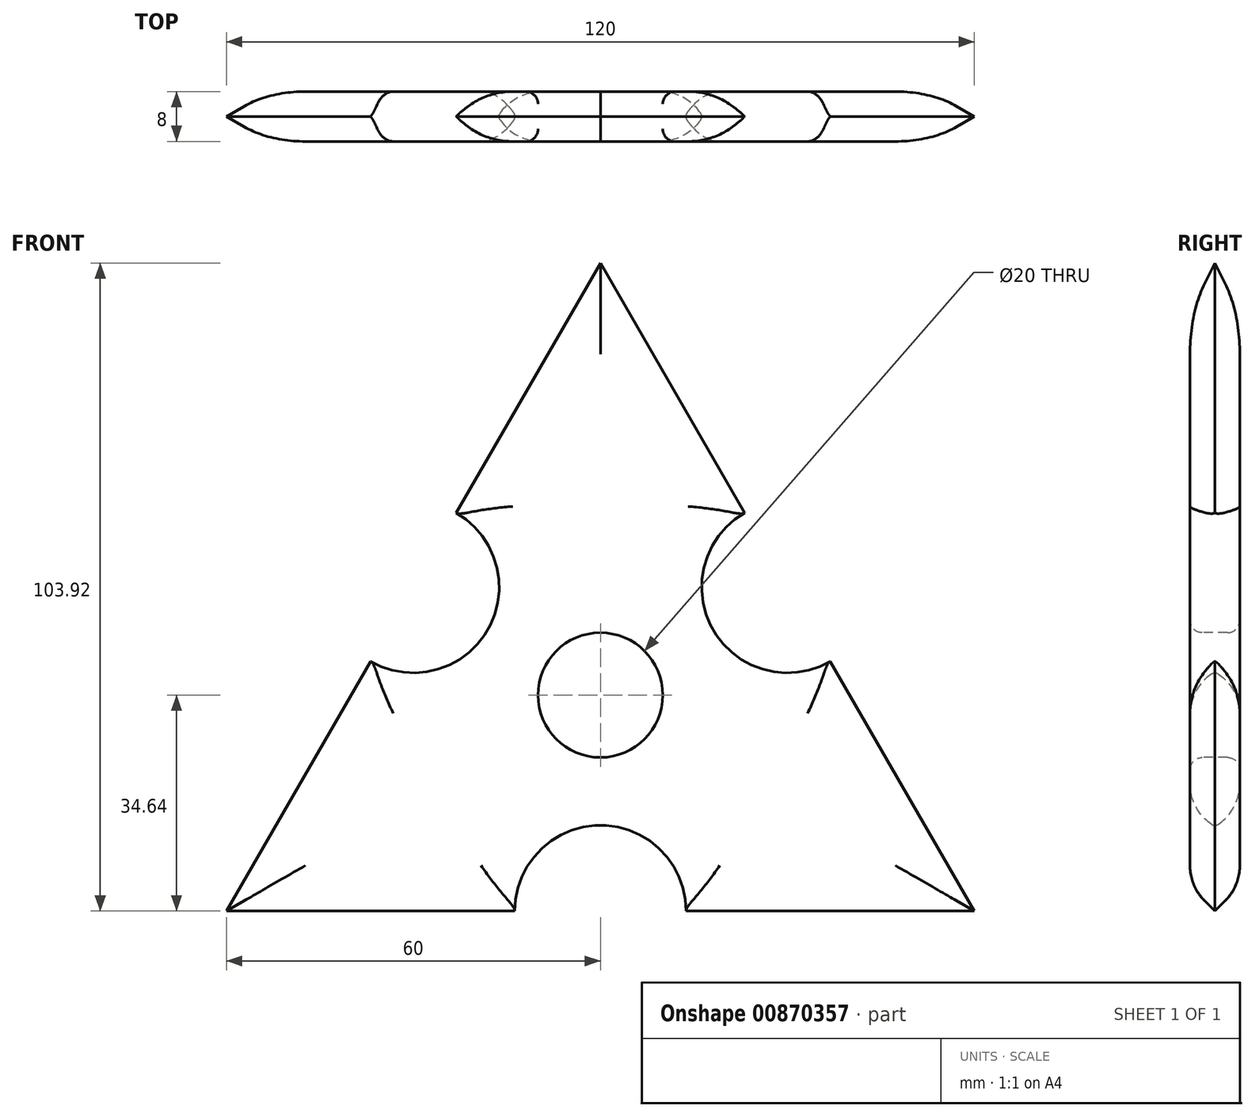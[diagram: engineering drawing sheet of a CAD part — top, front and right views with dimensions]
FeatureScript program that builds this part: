
annotation { "Feature Type Name" : "Feature", "Feature Type Description" : "" }
export const myFeature = defineFeature(function(context is Context, id is Id, definition is map)
    precondition{}
    {
        {
            var Q0;
            Q0=qCreatedBy(makeId("Front.planeOp"),FACE);
            var sketch = newSketch(context, id + "F0", { "sketchPlane" : qUnion([Q0])});
            skCircle(sketch, "E0.cCircle", {"center": v(0, 0) * mm, "radius": 69.28 * mm, "construction": true});
            skLineSegment(sketch, "E0.0", {"start": v(-60, -34.64) * mm, "end": v(0, 69.28) * mm});
            skLineSegment(sketch, "E0.1", {"start": v(0, 69.28) * mm, "end": v(60, -34.64) * mm});
            skLineSegment(sketch, "E0.2", {"start": v(60, -34.64) * mm, "end": v(-60, -34.64) * mm});
            skCircle(sketch, "E1", {"center": v(30, 17.32) * mm, "radius": 12.5 * mm});
            skCircle(sketch, "E2", {"center": v(-30, 17.32) * mm, "radius": 12.5 * mm});
            skCircle(sketch, "E3", {"center": v(0, -34.64) * mm, "radius": 12.5 * mm});
            skSolve(sketch);
        }
        {
            var Q0;
            {var subQ1=sQuery(id+"F0.wireOp",EDGE,"E0.0");var subQ8=sQuery(id+"F0.wireOp",EDGE,"E0.2");var subQ13=makeQuery(id+"F0.imprint","INTERSECT",VERTEX,{"derivedFrom":[subQ1,subQ8]});Q0=makeQuery(id+"F0.imprint","IMPRINT",FACE,{"disambiguationData":[TD([[makeQuery(id+"F0.imprint","IMPRINT",EDGE,{"disambiguationData":[TD([[subQ13,-1.0]])],"derivedFrom":subQ1}),-1.0]])]});}
            extrude(context, id + "F1", {"entities" : qUnion([Q0]), "depth" : 8 * mm, "offsetDistance" : 25 * mm, "symmetric" : true});
        }
        {
            var Q0;
            {var subQ0=sQuery(id+"F0.wireOp",EDGE,"E0.1");Q0=makeQuery(id+"F1.opExtrude","CAP_EDGE",EDGE,{"disambiguationData":[OSD([subQ0]),TDD([makeQuery(id+"F0.imprint","IMPRINT",EDGE,{"disambiguationData":[TD([[makeQuery(id+"F0.imprint","INTERSECT",VERTEX,{"derivedFrom":[sQuery(id+"F0.wireOp",EDGE,"E0.0"),subQ0]}),-1.0]])],"derivedFrom":subQ0})])],"isStart":true});}
            var Q1;
            {var subQ0=sQuery(id+"F0.wireOp",EDGE,"E0.0");Q1=makeQuery(id+"F1.opExtrude","CAP_EDGE",EDGE,{"disambiguationData":[OSD([subQ0]),TDD([makeQuery(id+"F0.imprint","IMPRINT",EDGE,{"disambiguationData":[TD([[makeQuery(id+"F0.imprint","INTERSECT",VERTEX,{"derivedFrom":[subQ0,sQuery(id+"F0.wireOp",EDGE,"E0.1")]}),1.0]])],"derivedFrom":subQ0})])],"isStart":true});}
            var Q2;
            {var subQ0=sQuery(id+"F0.wireOp",EDGE,"E0.0");Q2=makeQuery(id+"F1.opExtrude","CAP_EDGE",EDGE,{"disambiguationData":[OSD([subQ0]),TDD([makeQuery(id+"F0.imprint","IMPRINT",EDGE,{"disambiguationData":[TD([[makeQuery(id+"F0.imprint","INTERSECT",VERTEX,{"derivedFrom":[subQ0,sQuery(id+"F0.wireOp",EDGE,"E0.2")]}),-1.0]])],"derivedFrom":subQ0})])],"isStart":true});}
            var Q3;
            {var subQ0=sQuery(id+"F0.wireOp",EDGE,"E0.2");Q3=makeQuery(id+"F1.opExtrude","CAP_EDGE",EDGE,{"disambiguationData":[OSD([subQ0]),TDD([makeQuery(id+"F0.imprint","IMPRINT",EDGE,{"disambiguationData":[TD([[makeQuery(id+"F0.imprint","INTERSECT",VERTEX,{"derivedFrom":[sQuery(id+"F0.wireOp",EDGE,"E0.0"),subQ0]}),1.0]])],"derivedFrom":subQ0})])],"isStart":true});}
            var Q4;
            {var subQ0=sQuery(id+"F0.wireOp",EDGE,"E0.2");Q4=makeQuery(id+"F1.opExtrude","CAP_EDGE",EDGE,{"disambiguationData":[OSD([subQ0]),TDD([makeQuery(id+"F0.imprint","IMPRINT",EDGE,{"disambiguationData":[TD([[makeQuery(id+"F0.imprint","INTERSECT",VERTEX,{"derivedFrom":[sQuery(id+"F0.wireOp",EDGE,"E0.1"),subQ0]}),-1.0]])],"derivedFrom":subQ0})])],"isStart":true});}
            var Q5;
            {var subQ0=sQuery(id+"F0.wireOp",EDGE,"E0.1");Q5=makeQuery(id+"F1.opExtrude","CAP_EDGE",EDGE,{"disambiguationData":[OSD([subQ0]),TDD([makeQuery(id+"F0.imprint","IMPRINT",EDGE,{"disambiguationData":[TD([[makeQuery(id+"F0.imprint","INTERSECT",VERTEX,{"derivedFrom":[subQ0,sQuery(id+"F0.wireOp",EDGE,"E0.2")]}),1.0]])],"derivedFrom":subQ0})])],"isStart":true});}
            var Q6;
            {var subQ0=sQuery(id+"F0.wireOp",EDGE,"E0.2");Q6=makeQuery(id+"F1.opExtrude","CAP_EDGE",EDGE,{"disambiguationData":[OSD([subQ0]),TDD([makeQuery(id+"F0.imprint","IMPRINT",EDGE,{"disambiguationData":[TD([[makeQuery(id+"F0.imprint","INTERSECT",VERTEX,{"derivedFrom":[sQuery(id+"F0.wireOp",EDGE,"E0.1"),subQ0]}),-1.0]])],"derivedFrom":subQ0})])],"isStart":false});}
            var Q7;
            {var subQ0=sQuery(id+"F0.wireOp",EDGE,"E0.1");Q7=makeQuery(id+"F1.opExtrude","CAP_EDGE",EDGE,{"disambiguationData":[OSD([subQ0]),TDD([makeQuery(id+"F0.imprint","IMPRINT",EDGE,{"disambiguationData":[TD([[makeQuery(id+"F0.imprint","INTERSECT",VERTEX,{"derivedFrom":[subQ0,sQuery(id+"F0.wireOp",EDGE,"E0.2")]}),1.0]])],"derivedFrom":subQ0})])],"isStart":false});}
            var Q8;
            {var subQ0=sQuery(id+"F0.wireOp",EDGE,"E0.1");Q8=makeQuery(id+"F1.opExtrude","CAP_EDGE",EDGE,{"disambiguationData":[OSD([subQ0]),TDD([makeQuery(id+"F0.imprint","IMPRINT",EDGE,{"disambiguationData":[TD([[makeQuery(id+"F0.imprint","INTERSECT",VERTEX,{"derivedFrom":[sQuery(id+"F0.wireOp",EDGE,"E0.0"),subQ0]}),-1.0]])],"derivedFrom":subQ0})])],"isStart":false});}
            var Q9;
            {var subQ0=sQuery(id+"F0.wireOp",EDGE,"E0.0");Q9=makeQuery(id+"F1.opExtrude","CAP_EDGE",EDGE,{"disambiguationData":[OSD([subQ0]),TDD([makeQuery(id+"F0.imprint","IMPRINT",EDGE,{"disambiguationData":[TD([[makeQuery(id+"F0.imprint","INTERSECT",VERTEX,{"derivedFrom":[subQ0,sQuery(id+"F0.wireOp",EDGE,"E0.1")]}),1.0]])],"derivedFrom":subQ0})])],"isStart":false});}
            var Q10;
            {var subQ0=sQuery(id+"F0.wireOp",EDGE,"E0.0");Q10=makeQuery(id+"F1.opExtrude","CAP_EDGE",EDGE,{"disambiguationData":[OSD([subQ0]),TDD([makeQuery(id+"F0.imprint","IMPRINT",EDGE,{"disambiguationData":[TD([[makeQuery(id+"F0.imprint","INTERSECT",VERTEX,{"derivedFrom":[subQ0,sQuery(id+"F0.wireOp",EDGE,"E0.2")]}),-1.0]])],"derivedFrom":subQ0})])],"isStart":false});}
            var Q11;
            {var subQ0=sQuery(id+"F0.wireOp",EDGE,"E0.2");Q11=makeQuery(id+"F1.opExtrude","CAP_EDGE",EDGE,{"disambiguationData":[OSD([subQ0]),TDD([makeQuery(id+"F0.imprint","IMPRINT",EDGE,{"disambiguationData":[TD([[makeQuery(id+"F0.imprint","INTERSECT",VERTEX,{"derivedFrom":[sQuery(id+"F0.wireOp",EDGE,"E0.0"),subQ0]}),1.0]])],"derivedFrom":subQ0})])],"isStart":false});}
            chamfer(context, id + "F2", {"entities" : qUnion([Q0, Q1, Q2, Q3, Q4, Q5, Q6, Q7, Q8, Q9, Q10, Q11]), "width" : 4 * mm, "tangentPropagation" : true});
        }
        {
            var Q0;
            {var subQ0=sQuery(id+"F0.wireOp",EDGE,"E3");var subQ1=sQuery(id+"F0.wireOp",EDGE,"E0.2");var subQ2=sQuery(id+"F0.wireOp",EDGE,"E0.1");Q0=makeQuery(id+"F2.opChamfer","BLEND_EDGE",EDGE,{"blendedFrom":[makeQuery(id+"F1.opExtrude","CAP_EDGE",EDGE,{"disambiguationData":[OSD([subQ1]),TDD([makeQuery(id+"F0.imprint","IMPRINT",EDGE,{"disambiguationData":[TD([[makeQuery(id+"F0.imprint","INTERSECT",VERTEX,{"derivedFrom":[subQ2,subQ1]}),-1.0]])],"derivedFrom":subQ1})])],"isStart":false}),makeQuery(id+"F1.opExtrude","CAP_FACE",FACE,{"disambiguationData":[OSD([sQuery(id+"F0.wireOp",EDGE,"E0.0"),subQ2,subQ1,sQuery(id+"F0.wireOp",EDGE,"E1"),sQuery(id+"F0.wireOp",EDGE,"E2"),subQ0])],"isStart":false})],"blendedInto":[makeQuery(id+"F1.opExtrude","CAP_FACE",FACE,{"disambiguationData":[OSD([sQuery(id+"F0.wireOp",EDGE,"E0.0"),subQ2,subQ1,sQuery(id+"F0.wireOp",EDGE,"E1"),sQuery(id+"F0.wireOp",EDGE,"E2"),subQ0])],"isStart":false})]});}
            var Q1;
            {var subQ0=sQuery(id+"F0.wireOp",EDGE,"E1");var subQ1=sQuery(id+"F0.wireOp",EDGE,"E0.2");var subQ2=sQuery(id+"F0.wireOp",EDGE,"E0.1");Q1=makeQuery(id+"F2.opChamfer","BLEND_EDGE",EDGE,{"blendedFrom":[makeQuery(id+"F1.opExtrude","CAP_EDGE",EDGE,{"disambiguationData":[OSD([subQ2]),TDD([makeQuery(id+"F0.imprint","IMPRINT",EDGE,{"disambiguationData":[TD([[makeQuery(id+"F0.imprint","INTERSECT",VERTEX,{"derivedFrom":[subQ2,subQ1]}),1.0]])],"derivedFrom":subQ2})])],"isStart":false}),makeQuery(id+"F1.opExtrude","CAP_FACE",FACE,{"disambiguationData":[OSD([sQuery(id+"F0.wireOp",EDGE,"E0.0"),subQ2,subQ1,subQ0,sQuery(id+"F0.wireOp",EDGE,"E2"),sQuery(id+"F0.wireOp",EDGE,"E3")])],"isStart":false})],"blendedInto":[makeQuery(id+"F1.opExtrude","CAP_FACE",FACE,{"disambiguationData":[OSD([sQuery(id+"F0.wireOp",EDGE,"E0.0"),subQ2,subQ1,subQ0,sQuery(id+"F0.wireOp",EDGE,"E2"),sQuery(id+"F0.wireOp",EDGE,"E3")])],"isStart":false})]});}
            var Q2;
            Q2=makeQuery(id+"F1.opExtrude","CAP_EDGE",EDGE,{"disambiguationData":[OSD([sQuery(id+"F0.wireOp",EDGE,"E1")])],"isStart":false});
            var Q3;
            Q3=makeQuery(id+"F1.opExtrude","CAP_EDGE",EDGE,{"disambiguationData":[OSD([sQuery(id+"F0.wireOp",EDGE,"E3")])],"isStart":false});
            var Q4;
            {var subQ0=sQuery(id+"F0.wireOp",EDGE,"E3");var subQ1=sQuery(id+"F0.wireOp",EDGE,"E0.2");var subQ2=sQuery(id+"F0.wireOp",EDGE,"E0.0");Q4=makeQuery(id+"F2.opChamfer","BLEND_EDGE",EDGE,{"blendedFrom":[makeQuery(id+"F1.opExtrude","CAP_EDGE",EDGE,{"disambiguationData":[OSD([subQ1]),TDD([makeQuery(id+"F0.imprint","IMPRINT",EDGE,{"disambiguationData":[TD([[makeQuery(id+"F0.imprint","INTERSECT",VERTEX,{"derivedFrom":[subQ2,subQ1]}),1.0]])],"derivedFrom":subQ1})])],"isStart":false}),makeQuery(id+"F1.opExtrude","CAP_FACE",FACE,{"disambiguationData":[OSD([subQ2,sQuery(id+"F0.wireOp",EDGE,"E0.1"),subQ1,sQuery(id+"F0.wireOp",EDGE,"E1"),sQuery(id+"F0.wireOp",EDGE,"E2"),subQ0])],"isStart":false})],"blendedInto":[makeQuery(id+"F1.opExtrude","CAP_FACE",FACE,{"disambiguationData":[OSD([subQ2,sQuery(id+"F0.wireOp",EDGE,"E0.1"),subQ1,sQuery(id+"F0.wireOp",EDGE,"E1"),sQuery(id+"F0.wireOp",EDGE,"E2"),subQ0])],"isStart":false})]});}
            var Q5;
            {var subQ0=sQuery(id+"F0.wireOp",EDGE,"E2");var subQ1=sQuery(id+"F0.wireOp",EDGE,"E0.2");var subQ2=sQuery(id+"F0.wireOp",EDGE,"E0.0");Q5=makeQuery(id+"F2.opChamfer","BLEND_EDGE",EDGE,{"blendedFrom":[makeQuery(id+"F1.opExtrude","CAP_EDGE",EDGE,{"disambiguationData":[OSD([subQ2]),TDD([makeQuery(id+"F0.imprint","IMPRINT",EDGE,{"disambiguationData":[TD([[makeQuery(id+"F0.imprint","INTERSECT",VERTEX,{"derivedFrom":[subQ2,subQ1]}),-1.0]])],"derivedFrom":subQ2})])],"isStart":false}),makeQuery(id+"F1.opExtrude","CAP_FACE",FACE,{"disambiguationData":[OSD([subQ2,sQuery(id+"F0.wireOp",EDGE,"E0.1"),subQ1,sQuery(id+"F0.wireOp",EDGE,"E1"),subQ0,sQuery(id+"F0.wireOp",EDGE,"E3")])],"isStart":false})],"blendedInto":[makeQuery(id+"F1.opExtrude","CAP_FACE",FACE,{"disambiguationData":[OSD([subQ2,sQuery(id+"F0.wireOp",EDGE,"E0.1"),subQ1,sQuery(id+"F0.wireOp",EDGE,"E1"),subQ0,sQuery(id+"F0.wireOp",EDGE,"E3")])],"isStart":false})]});}
            var Q6;
            Q6=makeQuery(id+"F1.opExtrude","CAP_EDGE",EDGE,{"disambiguationData":[OSD([sQuery(id+"F0.wireOp",EDGE,"E2")])],"isStart":false});
            var Q7;
            {var subQ0=sQuery(id+"F0.wireOp",EDGE,"E2");var subQ1=sQuery(id+"F0.wireOp",EDGE,"E0.1");var subQ2=sQuery(id+"F0.wireOp",EDGE,"E0.0");Q7=makeQuery(id+"F2.opChamfer","BLEND_EDGE",EDGE,{"blendedFrom":[makeQuery(id+"F1.opExtrude","CAP_EDGE",EDGE,{"disambiguationData":[OSD([subQ2]),TDD([makeQuery(id+"F0.imprint","IMPRINT",EDGE,{"disambiguationData":[TD([[makeQuery(id+"F0.imprint","INTERSECT",VERTEX,{"derivedFrom":[subQ2,subQ1]}),1.0]])],"derivedFrom":subQ2})])],"isStart":false}),makeQuery(id+"F1.opExtrude","CAP_FACE",FACE,{"disambiguationData":[OSD([subQ2,subQ1,sQuery(id+"F0.wireOp",EDGE,"E0.2"),sQuery(id+"F0.wireOp",EDGE,"E1"),subQ0,sQuery(id+"F0.wireOp",EDGE,"E3")])],"isStart":false})],"blendedInto":[makeQuery(id+"F1.opExtrude","CAP_FACE",FACE,{"disambiguationData":[OSD([subQ2,subQ1,sQuery(id+"F0.wireOp",EDGE,"E0.2"),sQuery(id+"F0.wireOp",EDGE,"E1"),subQ0,sQuery(id+"F0.wireOp",EDGE,"E3")])],"isStart":false})]});}
            var Q8;
            {var subQ0=sQuery(id+"F0.wireOp",EDGE,"E1");var subQ1=sQuery(id+"F0.wireOp",EDGE,"E0.1");var subQ2=sQuery(id+"F0.wireOp",EDGE,"E0.0");Q8=makeQuery(id+"F2.opChamfer","BLEND_EDGE",EDGE,{"blendedFrom":[makeQuery(id+"F1.opExtrude","CAP_EDGE",EDGE,{"disambiguationData":[OSD([subQ1]),TDD([makeQuery(id+"F0.imprint","IMPRINT",EDGE,{"disambiguationData":[TD([[makeQuery(id+"F0.imprint","INTERSECT",VERTEX,{"derivedFrom":[subQ2,subQ1]}),-1.0]])],"derivedFrom":subQ1})])],"isStart":false}),makeQuery(id+"F1.opExtrude","CAP_FACE",FACE,{"disambiguationData":[OSD([subQ2,subQ1,sQuery(id+"F0.wireOp",EDGE,"E0.2"),subQ0,sQuery(id+"F0.wireOp",EDGE,"E2"),sQuery(id+"F0.wireOp",EDGE,"E3")])],"isStart":false})],"blendedInto":[makeQuery(id+"F1.opExtrude","CAP_FACE",FACE,{"disambiguationData":[OSD([subQ2,subQ1,sQuery(id+"F0.wireOp",EDGE,"E0.2"),subQ0,sQuery(id+"F0.wireOp",EDGE,"E2"),sQuery(id+"F0.wireOp",EDGE,"E3")])],"isStart":false})]});}
            var Q9;
            {var subQ0=sQuery(id+"F0.wireOp",EDGE,"E2");var subQ1=sQuery(id+"F0.wireOp",EDGE,"E0.2");var subQ2=sQuery(id+"F0.wireOp",EDGE,"E0.0");Q9=makeQuery(id+"F2.opChamfer","BLEND_EDGE",EDGE,{"blendedFrom":[makeQuery(id+"F1.opExtrude","CAP_EDGE",EDGE,{"disambiguationData":[OSD([subQ2]),TDD([makeQuery(id+"F0.imprint","IMPRINT",EDGE,{"disambiguationData":[TD([[makeQuery(id+"F0.imprint","INTERSECT",VERTEX,{"derivedFrom":[subQ2,subQ1]}),-1.0]])],"derivedFrom":subQ2})])],"isStart":true}),makeQuery(id+"F1.opExtrude","CAP_FACE",FACE,{"disambiguationData":[OSD([subQ2,sQuery(id+"F0.wireOp",EDGE,"E0.1"),subQ1,sQuery(id+"F0.wireOp",EDGE,"E1"),subQ0,sQuery(id+"F0.wireOp",EDGE,"E3")])],"isStart":true})],"blendedInto":[makeQuery(id+"F1.opExtrude","CAP_FACE",FACE,{"disambiguationData":[OSD([subQ2,sQuery(id+"F0.wireOp",EDGE,"E0.1"),subQ1,sQuery(id+"F0.wireOp",EDGE,"E1"),subQ0,sQuery(id+"F0.wireOp",EDGE,"E3")])],"isStart":true})]});}
            var Q10;
            {var subQ0=sQuery(id+"F0.wireOp",EDGE,"E2");var subQ1=sQuery(id+"F0.wireOp",EDGE,"E0.1");var subQ2=sQuery(id+"F0.wireOp",EDGE,"E0.0");Q10=makeQuery(id+"F2.opChamfer","BLEND_EDGE",EDGE,{"blendedFrom":[makeQuery(id+"F1.opExtrude","CAP_EDGE",EDGE,{"disambiguationData":[OSD([subQ2]),TDD([makeQuery(id+"F0.imprint","IMPRINT",EDGE,{"disambiguationData":[TD([[makeQuery(id+"F0.imprint","INTERSECT",VERTEX,{"derivedFrom":[subQ2,subQ1]}),1.0]])],"derivedFrom":subQ2})])],"isStart":true}),makeQuery(id+"F1.opExtrude","CAP_FACE",FACE,{"disambiguationData":[OSD([subQ2,subQ1,sQuery(id+"F0.wireOp",EDGE,"E0.2"),sQuery(id+"F0.wireOp",EDGE,"E1"),subQ0,sQuery(id+"F0.wireOp",EDGE,"E3")])],"isStart":true})],"blendedInto":[makeQuery(id+"F1.opExtrude","CAP_FACE",FACE,{"disambiguationData":[OSD([subQ2,subQ1,sQuery(id+"F0.wireOp",EDGE,"E0.2"),sQuery(id+"F0.wireOp",EDGE,"E1"),subQ0,sQuery(id+"F0.wireOp",EDGE,"E3")])],"isStart":true})]});}
            var Q11;
            Q11=makeQuery(id+"F1.opExtrude","CAP_EDGE",EDGE,{"disambiguationData":[OSD([sQuery(id+"F0.wireOp",EDGE,"E2")])],"isStart":true});
            var Q12;
            {var subQ0=sQuery(id+"F0.wireOp",EDGE,"E3");var subQ1=sQuery(id+"F0.wireOp",EDGE,"E0.2");var subQ2=sQuery(id+"F0.wireOp",EDGE,"E0.0");Q12=makeQuery(id+"F2.opChamfer","BLEND_EDGE",EDGE,{"blendedFrom":[makeQuery(id+"F1.opExtrude","CAP_EDGE",EDGE,{"disambiguationData":[OSD([subQ1]),TDD([makeQuery(id+"F0.imprint","IMPRINT",EDGE,{"disambiguationData":[TD([[makeQuery(id+"F0.imprint","INTERSECT",VERTEX,{"derivedFrom":[subQ2,subQ1]}),1.0]])],"derivedFrom":subQ1})])],"isStart":true}),makeQuery(id+"F1.opExtrude","CAP_FACE",FACE,{"disambiguationData":[OSD([subQ2,sQuery(id+"F0.wireOp",EDGE,"E0.1"),subQ1,sQuery(id+"F0.wireOp",EDGE,"E1"),sQuery(id+"F0.wireOp",EDGE,"E2"),subQ0])],"isStart":true})],"blendedInto":[makeQuery(id+"F1.opExtrude","CAP_FACE",FACE,{"disambiguationData":[OSD([subQ2,sQuery(id+"F0.wireOp",EDGE,"E0.1"),subQ1,sQuery(id+"F0.wireOp",EDGE,"E1"),sQuery(id+"F0.wireOp",EDGE,"E2"),subQ0])],"isStart":true})]});}
            var Q13;
            Q13=makeQuery(id+"F1.opExtrude","CAP_EDGE",EDGE,{"disambiguationData":[OSD([sQuery(id+"F0.wireOp",EDGE,"E3")])],"isStart":true});
            var Q14;
            {var subQ0=sQuery(id+"F0.wireOp",EDGE,"E3");var subQ1=sQuery(id+"F0.wireOp",EDGE,"E0.2");var subQ2=sQuery(id+"F0.wireOp",EDGE,"E0.1");Q14=makeQuery(id+"F2.opChamfer","BLEND_EDGE",EDGE,{"blendedFrom":[makeQuery(id+"F1.opExtrude","CAP_EDGE",EDGE,{"disambiguationData":[OSD([subQ1]),TDD([makeQuery(id+"F0.imprint","IMPRINT",EDGE,{"disambiguationData":[TD([[makeQuery(id+"F0.imprint","INTERSECT",VERTEX,{"derivedFrom":[subQ2,subQ1]}),-1.0]])],"derivedFrom":subQ1})])],"isStart":true}),makeQuery(id+"F1.opExtrude","CAP_FACE",FACE,{"disambiguationData":[OSD([sQuery(id+"F0.wireOp",EDGE,"E0.0"),subQ2,subQ1,sQuery(id+"F0.wireOp",EDGE,"E1"),sQuery(id+"F0.wireOp",EDGE,"E2"),subQ0])],"isStart":true})],"blendedInto":[makeQuery(id+"F1.opExtrude","CAP_FACE",FACE,{"disambiguationData":[OSD([sQuery(id+"F0.wireOp",EDGE,"E0.0"),subQ2,subQ1,sQuery(id+"F0.wireOp",EDGE,"E1"),sQuery(id+"F0.wireOp",EDGE,"E2"),subQ0])],"isStart":true})]});}
            var Q15;
            {var subQ0=sQuery(id+"F0.wireOp",EDGE,"E1");var subQ1=sQuery(id+"F0.wireOp",EDGE,"E0.2");var subQ2=sQuery(id+"F0.wireOp",EDGE,"E0.1");Q15=makeQuery(id+"F2.opChamfer","BLEND_EDGE",EDGE,{"blendedFrom":[makeQuery(id+"F1.opExtrude","CAP_EDGE",EDGE,{"disambiguationData":[OSD([subQ2]),TDD([makeQuery(id+"F0.imprint","IMPRINT",EDGE,{"disambiguationData":[TD([[makeQuery(id+"F0.imprint","INTERSECT",VERTEX,{"derivedFrom":[subQ2,subQ1]}),1.0]])],"derivedFrom":subQ2})])],"isStart":true}),makeQuery(id+"F1.opExtrude","CAP_FACE",FACE,{"disambiguationData":[OSD([sQuery(id+"F0.wireOp",EDGE,"E0.0"),subQ2,subQ1,subQ0,sQuery(id+"F0.wireOp",EDGE,"E2"),sQuery(id+"F0.wireOp",EDGE,"E3")])],"isStart":true})],"blendedInto":[makeQuery(id+"F1.opExtrude","CAP_FACE",FACE,{"disambiguationData":[OSD([sQuery(id+"F0.wireOp",EDGE,"E0.0"),subQ2,subQ1,subQ0,sQuery(id+"F0.wireOp",EDGE,"E2"),sQuery(id+"F0.wireOp",EDGE,"E3")])],"isStart":true})]});}
            var Q16;
            Q16=makeQuery(id+"F1.opExtrude","CAP_EDGE",EDGE,{"disambiguationData":[OSD([sQuery(id+"F0.wireOp",EDGE,"E1")])],"isStart":true});
            var Q17;
            {var subQ0=sQuery(id+"F0.wireOp",EDGE,"E1");var subQ1=sQuery(id+"F0.wireOp",EDGE,"E0.1");var subQ2=sQuery(id+"F0.wireOp",EDGE,"E0.0");Q17=makeQuery(id+"F2.opChamfer","BLEND_EDGE",EDGE,{"blendedFrom":[makeQuery(id+"F1.opExtrude","CAP_EDGE",EDGE,{"disambiguationData":[OSD([subQ1]),TDD([makeQuery(id+"F0.imprint","IMPRINT",EDGE,{"disambiguationData":[TD([[makeQuery(id+"F0.imprint","INTERSECT",VERTEX,{"derivedFrom":[subQ2,subQ1]}),-1.0]])],"derivedFrom":subQ1})])],"isStart":true}),makeQuery(id+"F1.opExtrude","CAP_FACE",FACE,{"disambiguationData":[OSD([subQ2,subQ1,sQuery(id+"F0.wireOp",EDGE,"E0.2"),subQ0,sQuery(id+"F0.wireOp",EDGE,"E2"),sQuery(id+"F0.wireOp",EDGE,"E3")])],"isStart":true})],"blendedInto":[makeQuery(id+"F1.opExtrude","CAP_FACE",FACE,{"disambiguationData":[OSD([subQ2,subQ1,sQuery(id+"F0.wireOp",EDGE,"E0.2"),subQ0,sQuery(id+"F0.wireOp",EDGE,"E2"),sQuery(id+"F0.wireOp",EDGE,"E3")])],"isStart":true})]});}
            fillet(context, id + "F3", {"entities" : qUnion([Q0, Q1, Q2, Q3, Q4, Q5, Q6, Q7, Q8, Q9, Q10, Q11, Q12, Q13, Q14, Q15, Q16, Q17]), "radius" : 8 * mm, "tangentPropagation" : true, "allowEdgeOverflow" : false});
        }
        {
            var Q0;
            Q0=makeQuery(id+"F1.opExtrude","CAP_FACE",FACE,{"disambiguationData":[OSD([sQuery(id+"F0.wireOp",EDGE,"E0.0"),sQuery(id+"F0.wireOp",EDGE,"E0.1"),sQuery(id+"F0.wireOp",EDGE,"E0.2"),sQuery(id+"F0.wireOp",EDGE,"E1"),sQuery(id+"F0.wireOp",EDGE,"E2"),sQuery(id+"F0.wireOp",EDGE,"E3")])],"isStart":false});
            var sketch = newSketch(context, id + "F4", { "sketchPlane" : qUnion([Q0])});
            skCircle(sketch, "E4", {"center": v(0, 0) * mm, "radius": 10 * mm});
            skSolve(sketch);
        }
        {
            var Q0;
            Q0=makeQuery(id+"F4.imprint","IMPRINT",FACE,{"disambiguationData":[TD([[makeQuery(id+"F4.imprint","IMPRINT",EDGE,{"derivedFrom":sQuery(id+"F4.wireOp",EDGE,"E4")}),1.0]])]});
            extrude(context, id + "F5", {"entities" : qUnion([Q0]), "operationType" : NewBodyOperationType.REMOVE, "oppositeDirection" : true, "depth" : 25 * mm, "offsetDistance" : 25 * mm, "symmetric" : true});
        }
        {
            var Q0;
            Q0=makeQuery(id+"F5.boolean.opBoolean","INTERSECT",EDGE,{"derivedFrom":[makeQuery(id+"F1.opExtrude","CAP_FACE",FACE,{"disambiguationData":[OSD([sQuery(id+"F0.wireOp",EDGE,"E0.0"),sQuery(id+"F0.wireOp",EDGE,"E0.1"),sQuery(id+"F0.wireOp",EDGE,"E0.2"),sQuery(id+"F0.wireOp",EDGE,"E1"),sQuery(id+"F0.wireOp",EDGE,"E2"),sQuery(id+"F0.wireOp",EDGE,"E3")])],"isStart":true}),makeQuery(id+"F5.opExtrude","SWEPT_FACE",FACE,{"disambiguationData":[OSD([sQuery(id+"F4.wireOp",EDGE,"E4")])]})]});
            var Q1;
            Q1=makeQuery(id+"F5.boolean.opBoolean","INTERSECT",EDGE,{"derivedFrom":[makeQuery(id+"F1.opExtrude","CAP_FACE",FACE,{"disambiguationData":[OSD([sQuery(id+"F0.wireOp",EDGE,"E0.0"),sQuery(id+"F0.wireOp",EDGE,"E0.1"),sQuery(id+"F0.wireOp",EDGE,"E0.2"),sQuery(id+"F0.wireOp",EDGE,"E1"),sQuery(id+"F0.wireOp",EDGE,"E2"),sQuery(id+"F0.wireOp",EDGE,"E3")])],"isStart":false}),makeQuery(id+"F5.opExtrude","SWEPT_FACE",FACE,{"disambiguationData":[OSD([sQuery(id+"F4.wireOp",EDGE,"E4")])]})]});
            fillet(context, id + "F6", {"entities" : qUnion([Q0, Q1]), "radius" : 2 * mm, "tangentPropagation" : true, "allowEdgeOverflow" : false});
        }
        {
            var Q0;
            {var subQ0=sQuery(id+"F0.wireOp",EDGE,"E1");Q0=makeQuery(id+"F3.opFillet","BLEND_EDGE",EDGE,{"blendedFrom":[makeQuery(id+"F1.opExtrude","CAP_EDGE",EDGE,{"disambiguationData":[OSD([subQ0])],"isStart":true}),makeQuery(id+"F1.opExtrude","CAP_EDGE",EDGE,{"disambiguationData":[OSD([subQ0])],"isStart":false})],"blendedInto":[]});}
            var Q1;
            {var subQ0=sQuery(id+"F0.wireOp",EDGE,"E3");Q1=makeQuery(id+"F3.opFillet","BLEND_EDGE",EDGE,{"blendedFrom":[makeQuery(id+"F1.opExtrude","CAP_EDGE",EDGE,{"disambiguationData":[OSD([subQ0])],"isStart":true}),makeQuery(id+"F1.opExtrude","CAP_EDGE",EDGE,{"disambiguationData":[OSD([subQ0])],"isStart":false})],"blendedInto":[]});}
            var Q2;
            {var subQ0=sQuery(id+"F0.wireOp",EDGE,"E2");Q2=makeQuery(id+"F3.opFillet","BLEND_EDGE",EDGE,{"blendedFrom":[makeQuery(id+"F1.opExtrude","CAP_EDGE",EDGE,{"disambiguationData":[OSD([subQ0])],"isStart":true}),makeQuery(id+"F1.opExtrude","CAP_EDGE",EDGE,{"disambiguationData":[OSD([subQ0])],"isStart":false})],"blendedInto":[]});}
            fillet(context, id + "F7", {"entities" : qUnion([Q0, Q1, Q2]), "radius" : 1 * mm, "tangentPropagation" : true, "allowEdgeOverflow" : false});
        }
    });
